# Revit family: FU_Table_Sandler_Essens_9-4
name_source: partatom
category: Furniture
units: mm (PartAtom-declared; Revit-internal decimal feet)

## family parameters
Always vertical = Yes
Cut with Voids When Loaded = No
OmniClass Number = 23.40.20.00
OmniClass Title = General Furniture and Specialties
Room Calculation Point = No
Shared = No
Work Plane-Based = No

## types (1)
- Essens 9.4
    Base Depth = 184 mm  [stored 0.603675 ft]
    Base Finish = PE2 - Concrete
    Base Width = 485 mm  [stored 1.59121 ft]
    Default Elevation = 0 mm  [stored 0 ft]
    Depth = 400 mm  [stored 1.31234 ft]
    Height = 720 mm  [stored 2.3622 ft]
    Section Depth = 140 mm  [stored 0.459318 ft]
    Section Width = 400 mm  [stored 1.31234 ft]
    Width = 700 mm  [stored 2.29659 ft]

note: [stored X ft] marks values corroborated as IEEE doubles in the binary element streams (Revit-internal decimal feet)

## geometry (parser evidence)
native form markers: Sweep x4
no freeform markers — native parametric forms only
